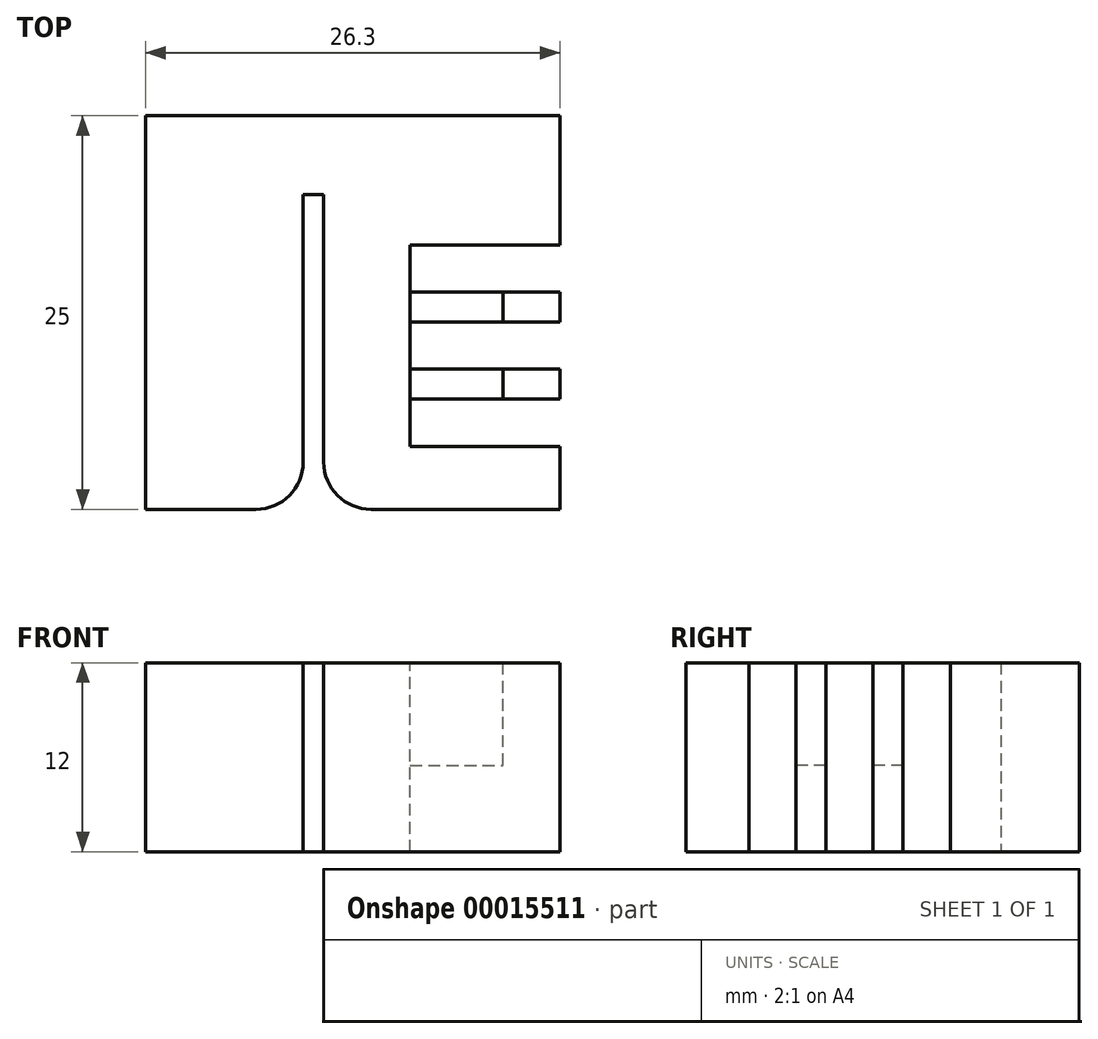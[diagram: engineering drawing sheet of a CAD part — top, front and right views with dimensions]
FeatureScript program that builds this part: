
annotation { "Feature Type Name" : "Feature", "Feature Type Description" : "" }
export const myFeature = defineFeature(function(context is Context, id is Id, definition is map)
    precondition{}
    {
        {
            var Q0;
            Q0=qCreatedBy(makeId("Top.planeOp"),FACE);
            var sketch = newSketch(context, id + "F0", { "sketchPlane" : qUnion([Q0])});
            skLineSegment(sketch, "E0.bottom", {"start": v(-11.3, 25) * mm, "end": v(15, 25) * mm});
            skLineSegment(sketch, "E0.top", {"start": v(-11.3, 0) * mm, "end": v(-1.3, 0) * mm});
            skLineSegment(sketch, "E0.left", {"start": v(-11.3, 25) * mm, "end": v(-11.3, 0) * mm});
            skLineSegment(sketch, "E0.right", {"start": v(15, 25) * mm, "end": v(15, 0) * mm});
            skLineSegment(sketch, "E1.top", {"start": v(-1.3, 20) * mm, "end": v(0, 20) * mm});
            skLineSegment(sketch, "E1.left", {"start": v(-1.3, 0) * mm, "end": v(-1.3, 20) * mm});
            skLineSegment(sketch, "E1.right", {"start": v(0, 0) * mm, "end": v(0, 20) * mm});
            skLineSegment(sketch, "E2.trimOffspring", {"start": v(0, 0) * mm, "end": v(15, 0) * mm});
            skLineSegment(sketch, "E3", {"start": v(0, 20) * mm, "end": v(0, 25) * mm});
            skSolve(sketch);
        }
        {
            var Q0;
            Q0=makeQuery(id+"F0.imprint","IMPRINT",FACE,{"disambiguationData":[TD([[makeQuery(id+"F0.imprint","IMPRINT",EDGE,{"derivedFrom":sQuery(id+"F0.wireOp",EDGE,"E0.top")}),1.0]])]});
            var Q1;
            {var subQ1=sQuery(id+"F0.wireOp",EDGE,"E0.right");Q1=makeQuery(id+"F0.imprint","IMPRINT",FACE,{"disambiguationData":[TD([[makeQuery(id+"F0.imprint","IMPRINT",EDGE,{"derivedFrom":subQ1}),-1.0]])]});}
            extrude(context, id + "F1", {"entities" : qUnion([Q0, Q1]), "depth" : 12 * mm});
        }
        {
            var Q0;
            Q0=makeQuery(id+"F1.opExtrude","CAP_FACE",FACE,{"disambiguationData":[OSD([sQuery(id+"F0.wireOp",EDGE,"E0.bottom"),sQuery(id+"F0.wireOp",EDGE,"E0.top"),sQuery(id+"F0.wireOp",EDGE,"E0.left"),sQuery(id+"F0.wireOp",EDGE,"E0.right"),sQuery(id+"F0.wireOp",EDGE,"E1.top"),sQuery(id+"F0.wireOp",EDGE,"E1.left"),sQuery(id+"F0.wireOp",EDGE,"E1.right"),sQuery(id+"F0.wireOp",EDGE,"E2.trimOffspring")])],"isStart":false});
            var sketch = newSketch(context, id + "F2", { "sketchPlane" : qUnion([Q0])});
            skLineSegment(sketch, "E4.bottom", {"start": v(5.5, 16.8) * mm, "end": v(11.4, 16.8) * mm});
            skLineSegment(sketch, "E4.top", {"start": v(5.5, 4) * mm, "end": v(11.4, 4) * mm});
            skLineSegment(sketch, "E4.left", {"start": v(5.5, 16.8) * mm, "end": v(5.5, 4) * mm});
            skLineSegment(sketch, "E4.right", {"start": v(11.4, 16.8) * mm, "end": v(11.4, 4) * mm});
            skLineSegment(sketch, "E5", {"start": v(11.4, 4) * mm, "end": v(15, 4) * mm});
            skSolve(sketch);
        }
        {
            var Q0;
            Q0 = qSketchRegion(id + "F2", true);
            extrude(context, id + "F3", {"entities" : qUnion([Q0]), "operationType" : NewBodyOperationType.REMOVE, "oppositeDirection" : true, "depth" : 6.5 * mm});
        }
        {
            var Q0;
            Q0=makeQuery(id+"F1.opExtrude","CAP_FACE",FACE,{"disambiguationData":[OSD([sQuery(id+"F0.wireOp",EDGE,"E0.bottom"),sQuery(id+"F0.wireOp",EDGE,"E0.top"),sQuery(id+"F0.wireOp",EDGE,"E0.left"),sQuery(id+"F0.wireOp",EDGE,"E0.right"),sQuery(id+"F0.wireOp",EDGE,"E1.top"),sQuery(id+"F0.wireOp",EDGE,"E1.left"),sQuery(id+"F0.wireOp",EDGE,"E1.right"),sQuery(id+"F0.wireOp",EDGE,"E2.trimOffspring")])],"isStart":false});
            var sketch = newSketch(context, id + "F4", { "sketchPlane" : qUnion([Q0])});
            skLineSegment(sketch, "E6.bottom", {"start": v(5.5, 16.8) * mm, "end": v(15, 16.8) * mm});
            skLineSegment(sketch, "E6.top", {"start": v(5.5, 13.8) * mm, "end": v(15, 13.8) * mm});
            skLineSegment(sketch, "E6.left", {"start": v(5.5, 16.8) * mm, "end": v(5.5, 13.8) * mm});
            skLineSegment(sketch, "E6.right", {"start": v(15, 16.8) * mm, "end": v(15, 13.8) * mm});
            skLineSegment(sketch, "E7.bottom", {"start": v(5.5, 4) * mm, "end": v(15, 4) * mm});
            skLineSegment(sketch, "E7.top", {"start": v(5.5, 7) * mm, "end": v(15, 7) * mm});
            skLineSegment(sketch, "E7.left", {"start": v(5.5, 4) * mm, "end": v(5.5, 7) * mm});
            skLineSegment(sketch, "E7.right", {"start": v(15, 4) * mm, "end": v(15, 7) * mm});
            skLineSegment(sketch, "E8.bottom", {"start": v(5.5, 8.9) * mm, "end": v(15, 8.9) * mm});
            skLineSegment(sketch, "E8.top", {"start": v(5.5, 11.9) * mm, "end": v(15, 11.9) * mm});
            skLineSegment(sketch, "E8.left", {"start": v(5.5, 8.9) * mm, "end": v(5.5, 11.9) * mm});
            skLineSegment(sketch, "E8.right", {"start": v(15, 8.9) * mm, "end": v(15, 11.9) * mm});
            skLineSegment(sketch, "E9", {"start": v(5.5, 11.9) * mm, "end": v(5.5, 13.8) * mm});
            skLineSegment(sketch, "E10", {"start": v(5.5, 7) * mm, "end": v(5.5, 8.9) * mm});
            skSolve(sketch);
        }
        {
            var Q0;
            Q0 = qSketchRegion(id + "F4", true);
            extrude(context, id + "F5", {"entities" : qUnion([Q0]), "operationType" : NewBodyOperationType.REMOVE, "endBound" : BoundingType.THROUGH_ALL, "oppositeDirection" : true, "depth" : 25 * mm});
        }
        {
            var Q0;
            Q0=makeQuery(id+"F1.opExtrude","SWEPT_EDGE",EDGE,{"disambiguationData":[OSD([sQuery(id+"F0.wireOp",EDGE,"E0.top"),sQuery(id+"F0.wireOp",EDGE,"E1.left")])]});
            var Q1;
            Q1=makeQuery(id+"F1.opExtrude","SWEPT_EDGE",EDGE,{"disambiguationData":[OSD([sQuery(id+"F0.wireOp",EDGE,"E1.right"),sQuery(id+"F0.wireOp",EDGE,"E2.trimOffspring")])]});
            fillet(context, id + "F6", {"entities" : qUnion([Q0, Q1]), "radius" : 3 * mm, "tangentPropagation" : true, "allowEdgeOverflow" : false});
        }
    });
